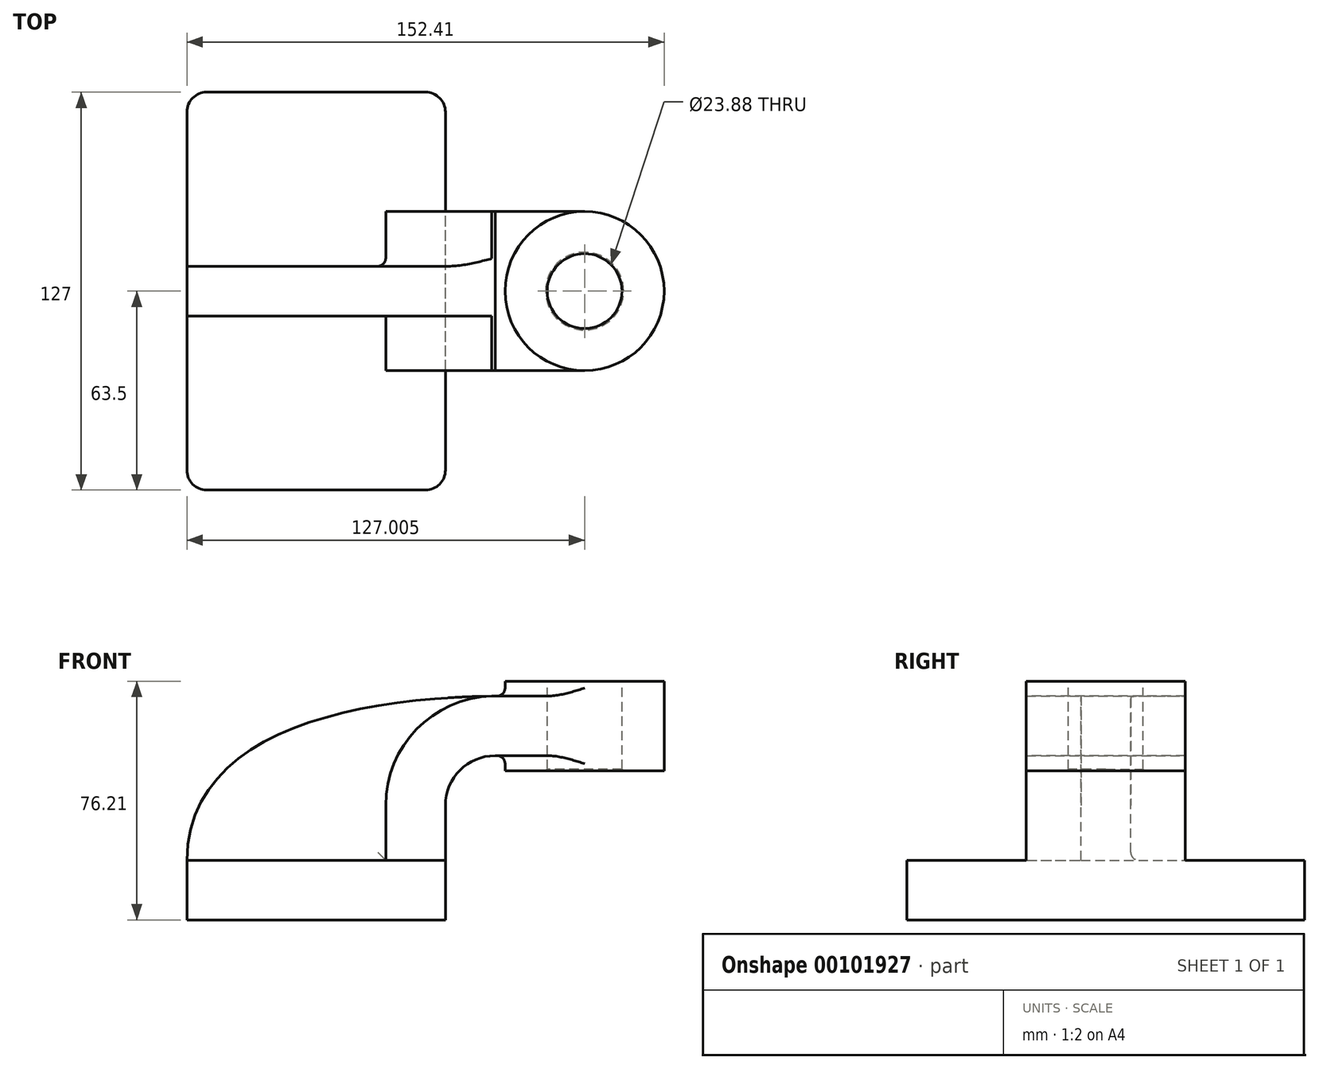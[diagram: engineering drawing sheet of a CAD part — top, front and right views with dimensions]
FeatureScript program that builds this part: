
annotation { "Feature Type Name" : "Feature", "Feature Type Description" : "" }
export const myFeature = defineFeature(function(context is Context, id is Id, definition is map)
    precondition{}
    {
        {
            var Q0;
            Q0=qCreatedBy(makeId("Front.planeOp"),FACE);
            var sketch = newSketch(context, id + "F0", { "sketchPlane" : qUnion([Q0])});
            skLineSegment(sketch, "E0.bottom", {"start": v(-41.27, -9.53) * mm, "end": v(41.28, -9.53) * mm});
            skLineSegment(sketch, "E0.top", {"start": v(-41.28, 9.52) * mm, "end": v(41.28, 9.52) * mm});
            skLineSegment(sketch, "E0.left", {"start": v(-41.28, -9.53) * mm, "end": v(-41.28, 9.53) * mm});
            skLineSegment(sketch, "E0.right", {"start": v(41.28, -9.53) * mm, "end": v(41.28, 9.52) * mm});
            skPoint(sketch, "E0.middle", {"position": v(0, 0) * mm});
            skLineSegment(sketch, "E1.bottom", {"start": v(60.33, 38.1) * mm, "end": v(111.13, 38.1) * mm});
            skLineSegment(sketch, "E1.top", {"start": v(60.32, 66.68) * mm, "end": v(111.13, 66.68) * mm});
            skLineSegment(sketch, "E1.left", {"start": v(60.33, 38.1) * mm, "end": v(60.32, 66.68) * mm});
            skLineSegment(sketch, "E1.right", {"start": v(111.13, 38.1) * mm, "end": v(111.12, 66.68) * mm});
            skPoint(sketch, "E1.middle", {"position": v(85.73, 52.39) * mm});
            skLineSegment(sketch, "E2", {"start": v(41.28, 9.52) * mm, "end": v(41.28, 27) * mm});
            skArc(sketch, "E3", {"start": v(41.27, 27) * mm, "mid": v(45.92, 38.23) * mm, "end": v(57.15, 42.88) * mm});
            skLineSegment(sketch, "E4", {"start": v(57.15, 42.88) * mm, "end": v(85.73, 42.88) * mm});
            skLineSegment(sketch, "E5.0", {"start": v(57.15, 61.93) * mm, "end": v(85.73, 61.93) * mm});
            skArc(sketch, "E5.1", {"start": v(22.22, 27) * mm, "mid": v(32.45, 51.7) * mm, "end": v(57.15, 61.93) * mm});
            skLineSegment(sketch, "E5.2", {"start": v(22.22, 9.52) * mm, "end": v(22.22, 27) * mm});
            skLineSegment(sketch, "E6", {"start": v(85.72, 38.1) * mm, "end": v(85.72, 66.68) * mm});
            skFitSpline(sketch, "E7", {"points": [v(-41.28, 9.53) * mm, v(57.15, 61.93) * mm], "startDerivative": vector(1.51, 122.45) * mm, "endDerivative": vector(139.7, 1.86) * mm});
            skSolve(sketch);
        }
        {
            var Q0;
            Q0=makeQuery(id+"F0.imprint","IMPRINT",FACE,{"disambiguationData":[TD([[makeQuery(id+"F0.imprint","IMPRINT",EDGE,{"derivedFrom":sQuery(id+"F0.wireOp",EDGE,"E0.bottom")}),1.0]])]});
            extrude(context, id + "F1", {"entities" : qUnion([Q0]), "endBound" : BoundingType.SYMMETRIC, "depth" : 127 * mm});
        }
        {
            var Q0;
            {var subQ1=sQuery(id+"F0.wireOp",EDGE,"E2");Q0=makeQuery(id+"F0.imprint","IMPRINT",FACE,{"disambiguationData":[TD([[makeQuery(id+"F0.imprint","IMPRINT",EDGE,{"derivedFrom":subQ1}),1.0]])]});}
            var Q1;
            {var subQ0=sQuery(id+"F0.wireOp",EDGE,"E4");var subQ1=sQuery(id+"F0.wireOp",EDGE,"E1.left");var subQ2=makeQuery(id+"F0.imprint","INTERSECT",VERTEX,{"derivedFrom":[subQ1,subQ0]});Q1=makeQuery(id+"F0.imprint","IMPRINT",FACE,{"disambiguationData":[TD([[makeQuery(id+"F0.imprint","IMPRINT",EDGE,{"disambiguationData":[TD([[subQ2,-1.0]])],"derivedFrom":subQ1}),-1.0]])]});}
            extrude(context, id + "F2", {"entities" : qUnion([Q0, Q1]), "operationType" : NewBodyOperationType.ADD, "endBound" : BoundingType.SYMMETRIC, "depth" : 50.8 * mm});
        }
        {
            var Q0;
            {var subQ0=sQuery(id+"F0.wireOp",EDGE,"E1.right");Q0=makeQuery(id+"F0.imprint","IMPRINT",FACE,{"disambiguationData":[TD([[makeQuery(id+"F0.imprint","IMPRINT",EDGE,{"derivedFrom":subQ0}),1.0]])]});}
            var Q1;
            Q1=sQuery(id+"F0.wireOp",EDGE,"E6");
            revolve(context, id + "F3", {"operationType" : NewBodyOperationType.ADD, "entities" : qUnion([Q0]), "axis" : qUnion([Q1]), "revolveType" : RevolveType.FULL});
        }
        {
            var Q0;
            {var subQ3=sQuery(id+"F0.wireOp",EDGE,"E5.2");Q0=makeQuery(id+"F0.imprint","IMPRINT",FACE,{"disambiguationData":[TD([[makeQuery(id+"F0.imprint","IMPRINT",EDGE,{"derivedFrom":subQ3}),1.0]])]});}
            extrude(context, id + "F4", {"entities" : qUnion([Q0]), "operationType" : NewBodyOperationType.ADD, "endBound" : BoundingType.SYMMETRIC, "depth" : 15.88 * mm});
        }
        {
            var Q0;
            Q0=makeQuery(id+"F1.opExtrude","CAP_EDGE",EDGE,{"disambiguationData":[OSD([sQuery(id+"F0.wireOp",EDGE,"E0.left")])],"isStart":false});
            var Q1;
            Q1=makeQuery(id+"F1.opExtrude","CAP_EDGE",EDGE,{"disambiguationData":[OSD([sQuery(id+"F0.wireOp",EDGE,"E0.right")])],"isStart":false});
            var Q2;
            Q2=makeQuery(id+"F1.opExtrude","CAP_EDGE",EDGE,{"disambiguationData":[OSD([sQuery(id+"F0.wireOp",EDGE,"E0.right")])],"isStart":true});
            var Q3;
            Q3=makeQuery(id+"F1.opExtrude","CAP_EDGE",EDGE,{"disambiguationData":[OSD([sQuery(id+"F0.wireOp",EDGE,"E0.left")])],"isStart":true});
            fillet(context, id + "F5", {"entities" : qUnion([Q0, Q1, Q2, Q3]), "radius" : 6.35 * mm, "tangentPropagation" : true, "allowEdgeOverflow" : false});
        }
        {
            var Q0;
            Q0=makeQuery(id+"F4.opExtrude","CAP_EDGE",EDGE,{"disambiguationData":[OSD([sQuery(id+"F0.wireOp",EDGE,"E0.top")])],"isStart":false});
            var Q1;
            {var subQ0=sQuery(id+"F0.wireOp",EDGE,"E0.top");var subQ1=sQuery(id+"F0.wireOp",EDGE,"E7");var subQ2=sQuery(id+"F0.wireOp",EDGE,"E5.2");var subQ3=sQuery(id+"F0.wireOp",EDGE,"E5.1");Q1=makeQuery(id+"F4.boolean.opBoolean","SPLIT",EDGE,{"disambiguationData":[TD([makeQuery(id+"F4.opExtrude","CAP_FACE",FACE,{"disambiguationData":[OSD([subQ0,subQ3,subQ2,subQ1])],"isStart":false})])],"derivedFrom":makeQuery(id+"F2.opExtrude","SWEPT_EDGE",EDGE,{"disambiguationData":[OSD([subQ0,subQ2])]})});}
            var Q2;
            Q2=makeQuery(id+"F2.opExtrude","CAP_EDGE",EDGE,{"disambiguationData":[OSD([sQuery(id+"F0.wireOp",EDGE,"E0.top")])],"isStart":false});
            var Q3;
            Q3=makeQuery(id+"F4.opExtrude","CAP_EDGE",EDGE,{"disambiguationData":[OSD([sQuery(id+"F0.wireOp",EDGE,"E5.1")])],"isStart":false});
            var Q4;
            Q4=makeQuery(id+"F3.boolean.opBoolean","INTERSECT",EDGE,{"derivedFrom":[makeQuery(id+"F2.opExtrude","SWEPT_FACE",FACE,{"disambiguationData":[OSD([sQuery(id+"F0.wireOp",EDGE,"E5.0")])]}),makeQuery(id+"F3.opRevolve","SWEPT_FACE",FACE,{"disambiguationData":[OSD([sQuery(id+"F0.wireOp",EDGE,"E1.right")])]})]});
            var Q5;
            Q5=makeQuery(id+"F3.boolean.opBoolean","INTERSECT",EDGE,{"derivedFrom":[makeQuery(id+"F2.opExtrude","SWEPT_FACE",FACE,{"disambiguationData":[OSD([sQuery(id+"F0.wireOp",EDGE,"E4")])]}),makeQuery(id+"F3.opRevolve","SWEPT_FACE",FACE,{"disambiguationData":[OSD([sQuery(id+"F0.wireOp",EDGE,"E1.right")])]})]});
            var Q6;
            Q6=makeQuery(id+"F4.opExtrude","CAP_EDGE",EDGE,{"disambiguationData":[OSD([sQuery(id+"F0.wireOp",EDGE,"E0.top")])],"isStart":true});
            var Q7;
            Q7=makeQuery(id+"F4.opExtrude","CAP_EDGE",EDGE,{"disambiguationData":[OSD([sQuery(id+"F0.wireOp",EDGE,"E5.2")])],"isStart":true});
            var Q8;
            Q8=makeQuery(id+"F4.opExtrude","CAP_EDGE",EDGE,{"disambiguationData":[OSD([sQuery(id+"F0.wireOp",EDGE,"E5.1")])],"isStart":true});
            fillet(context, id + "F6", {"entities" : qUnion([Q0, Q1, Q2, Q3, Q4, Q5, Q6, Q7, Q8]), "radius" : 2.54 * mm, "tangentPropagation" : true, "allowEdgeOverflow" : false});
        }
        {
            var Q0;
            Q0=makeQuery(id+"F3.opRevolve","SWEPT_FACE",FACE,{"disambiguationData":[OSD([sQuery(id+"F0.wireOp",EDGE,"E1.top")])]});
            var sketch = newSketch(context, id + "F7", { "sketchPlane" : qUnion([Q0])});
            skCircle(sketch, "E8", {"center": v(85.72, 0) * mm, "radius": 11.94 * mm});
            skSolve(sketch);
        }
        {
            var Q0;
            Q0 = qSketchRegion(id + "F7", true);
            extrude(context, id + "F8", {"entities" : qUnion([Q0]), "operationType" : NewBodyOperationType.REMOVE, "endBound" : BoundingType.THROUGH_ALL, "oppositeDirection" : true, "depth" : 25.4 * mm});
        }
        {
            var Q0;
            Q0=makeQuery(id+"F8.boolean.opBoolean","COPY",EDGE,{"derivedFrom":makeQuery(id+"F8.opExtrude","CAP_EDGE",EDGE,{"disambiguationData":[OSD([sQuery(id+"F7.wireOp",EDGE,"E8")])],"isStart":true})});
            var Q1;
            Q1=makeQuery(id+"F8.boolean.opBoolean","INTERSECT",EDGE,{"derivedFrom":[makeQuery(id+"F3.opRevolve","SWEPT_FACE",FACE,{"disambiguationData":[OSD([sQuery(id+"F0.wireOp",EDGE,"E1.bottom")])]}),makeQuery(id+"F8.opExtrude","SWEPT_FACE",FACE,{"disambiguationData":[OSD([sQuery(id+"F7.wireOp",EDGE,"E8")])]})]});
            chamfer(context, id + "F9", {"entities" : qUnion([Q0, Q1]), "width" : 0.5 * mm, "tangentPropagation" : true});
        }
    });
